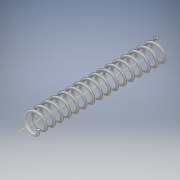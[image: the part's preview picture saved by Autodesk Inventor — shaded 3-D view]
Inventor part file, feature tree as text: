
AUTODESK INVENTOR PART (.ipt)
format: ipt  version: 2018 (Build 220112000, 112)  size: 310,784 bytes
history: native  units: mm
features: sketch x2, helix x1, other x1
ambient origin geometry x8: Origin, YZ Plane, XZ Plane, XY Plane, X Axis, Y Axis, Z Axis, Center Point
bodies: Solid1 (feature_tree)
feature tree (4):
  helix  "Coil1"  [1 undecoded]
  sketch  "Sketch2"  dims[d2=1.6mm d3=1.5mm d4=25.0mm d5=10.0mm d6=0.0mm d7=90.0deg d8=90.0deg d9=0.0mm d10=0.0mm]
  other  "Work Axis1"
  sketch  "Sketch1"  dims[d1=0.5mm]
note: 1 required parameter value undecoded (feature->parameter linkage not recoverable at this tier; creation-order binding heuristic only, values carry confidence <= 0.55)
